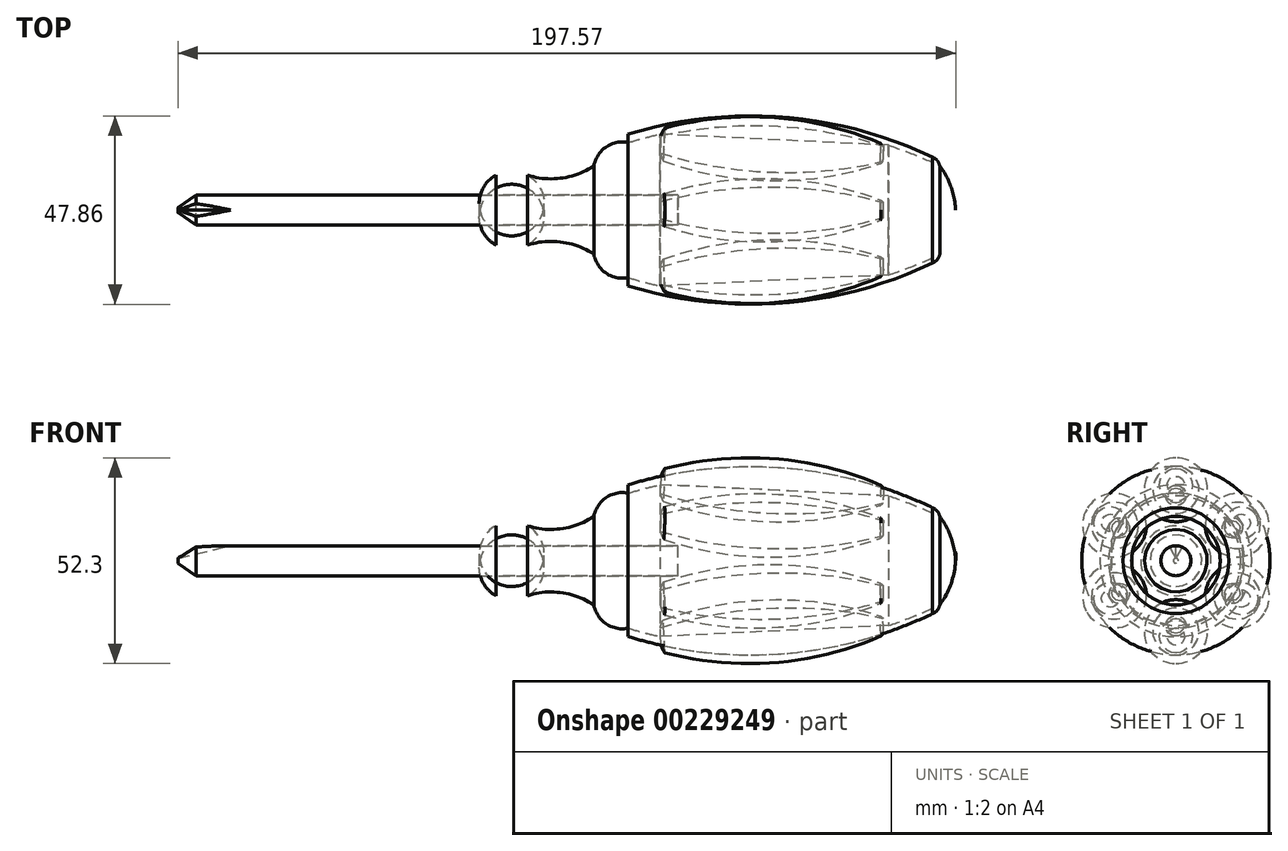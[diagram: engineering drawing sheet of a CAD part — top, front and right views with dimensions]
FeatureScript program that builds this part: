
annotation { "Feature Type Name" : "Feature", "Feature Type Description" : "" }
export const myFeature = defineFeature(function(context is Context, id is Id, definition is map)
    precondition{}
    {
        {
            var Q0;
            Q0=qCreatedBy(makeId("Front.planeOp"),FACE);
            var sketch = newSketch(context, id + "F0", { "sketchPlane" : qUnion([Q0])});
            skLineSegment(sketch, "E0", {"start": v(-80.73, 0) * mm, "end": v(-80.73, 0.63) * mm});
            skLineSegment(sketch, "E1", {"start": v(-80.73, 0.63) * mm, "end": v(-76.2, 3.8) * mm});
            skLineSegment(sketch, "E2", {"start": v(-76.2, 3.8) * mm, "end": v(46.27, 3.8) * mm});
            skLineSegment(sketch, "E3", {"start": v(46.27, 3.8) * mm, "end": v(46.27, 0) * mm});
            skLineSegment(sketch, "E4", {"start": v(46.27, 0) * mm, "end": v(-80.73, 0) * mm});
            skLineSegment(sketch, "E5", {"start": v(0, 3.8) * mm, "end": v(0, 8.89) * mm});
            skArc(sketch, "E6", {"start": v(8.04, 8.89) * mm, "mid": v(4.02, 9.93) * mm, "end": v(0, 8.89) * mm});
            skArc(sketch, "E7", {"start": v(8.04, 8.89) * mm, "mid": v(16.73, 8.13) * mm, "end": v(24.89, 11.25) * mm});
            skArc(sketch, "E8", {"start": v(33.62, 17.15) * mm, "mid": v(28, 16.04) * mm, "end": v(24.89, 11.25) * mm});
            skArc(sketch, "E9", {"start": v(112.77, 11.25) * mm, "mid": v(73.75, 21.64) * mm, "end": v(33.62, 17.15) * mm});
            skArc(sketch, "E10", {"start": v(116.81, 0) * mm, "mid": v(115.61, 5.92) * mm, "end": v(112.77, 11.25) * mm});
            skLineSegment(sketch, "E11", {"start": v(33.62, 17.15) * mm, "end": v(33.62, 19.29) * mm});
            skArc(sketch, "E12", {"start": v(110.93, 13.46) * mm, "mid": v(72.82, 23.62) * mm, "end": v(33.62, 19.29) * mm});
            skArc(sketch, "E13", {"start": v(42.94, 23.4) * mm, "mid": v(41.95, 21.46) * mm, "end": v(41.69, 19.29) * mm});
            skArc(sketch, "E14", {"start": v(97.82, 19.15) * mm, "mid": v(70.74, 25.9) * mm, "end": v(42.94, 23.4) * mm});
            skArc(sketch, "E15", {"start": v(99.75, 16.47) * mm, "mid": v(98.95, 17.93) * mm, "end": v(97.82, 19.15) * mm});
            skLineSegment(sketch, "E16", {"start": v(41.69, 19.29) * mm, "end": v(99.75, 16.47) * mm});
            skLineSegment(sketch, "E17", {"start": v(46.27, 0) * mm, "end": v(116.81, 0) * mm});
            skLineSegment(sketch, "E18", {"start": v(8.04, 8.89) * mm, "end": v(8.04, 3.8) * mm, "construction": true});
            skLineSegment(sketch, "E19", {"start": v(24.89, 11.25) * mm, "end": v(24.89, 3.8) * mm, "construction": true});
            skLineSegment(sketch, "E20", {"start": v(33.62, 17.15) * mm, "end": v(33.62, 3.8) * mm, "construction": true});
            skArc(sketch, "E21", {"start": v(112.77, 11.25) * mm, "mid": v(112.13, 12.59) * mm, "end": v(110.93, 13.46) * mm});
            skLineSegment(sketch, "E22", {"start": v(112.77, 11.25) * mm, "end": v(112.77, 0) * mm, "construction": true});
            skLineSegment(sketch, "E23", {"start": v(48.03, 19.6) * mm, "end": v(48.03, 0) * mm, "construction": true});
            skLineSegment(sketch, "E24", {"start": v(42.94, 23.4) * mm, "end": v(42.94, 0) * mm, "construction": true});
            skLineSegment(sketch, "E25", {"start": v(97.82, 19.15) * mm, "end": v(97.82, 0) * mm, "construction": true});
            skLineSegment(sketch, "E26", {"start": v(110.93, 13.46) * mm, "end": v(110.93, 0) * mm, "construction": true});
            skSolve(sketch);
        }
        {
            var Q0;
            {var subQ5=sQuery(id+"F0.wireOp",EDGE,"E14");Q0=makeQuery(id+"F0.imprint","IMPRINT",FACE,{"disambiguationData":[TD([[makeQuery(id+"F0.imprint","IMPRINT",EDGE,{"derivedFrom":subQ5}),1.0]])]});}
            var Q1;
            Q1=sQuery(id+"F0.wireOp",EDGE,"E16");
            revolve(context, id + "F1", {"entities" : qUnion([Q0]), "axis" : qUnion([Q1]), "revolveType" : RevolveType.FULL});
        }
        {
            var Q0;
            Q0=makeQuery(id+"F0.imprint","IMPRINT",FACE,{"disambiguationData":[TD([[makeQuery(id+"F0.imprint","IMPRINT",EDGE,{"derivedFrom":sQuery(id+"F0.wireOp",EDGE,"E0")}),-1.0]])]});
            var Q1;
            Q1=sQuery(id+"F0.wireOp",EDGE,"E4");
            revolve(context, id + "F2", {"entities" : qUnion([Q0]), "axis" : qUnion([Q1]), "revolveType" : RevolveType.FULL});
        }
        {
            var Q0;
            {var subQ3=sQuery(id+"F0.wireOp",EDGE,"E3");Q0=makeQuery(id+"F0.imprint","IMPRINT",FACE,{"disambiguationData":[TD([[makeQuery(id+"F0.imprint","IMPRINT",EDGE,{"derivedFrom":subQ3}),1.0]])]});}
            var Q1;
            Q1=sQuery(id+"F0.wireOp",EDGE,"E17");
            revolve(context, id + "F3", {"entities" : qUnion([Q0]), "axis" : qUnion([Q1]), "revolveType" : RevolveType.FULL});
        }
        {
            var Q0;
            {var subQ0=sQuery(id+"F0.wireOp",EDGE,"E11");Q0=makeQuery(id+"F0.imprint","IMPRINT",FACE,{"disambiguationData":[TD([[makeQuery(id+"F0.imprint","IMPRINT",EDGE,{"derivedFrom":subQ0}),-1.0]])]});}
            var Q1;
            {var subQ0=sQuery(id+"F0.wireOp",EDGE,"E16");Q1=makeQuery(id+"F0.imprint","IMPRINT",FACE,{"disambiguationData":[TD([[makeQuery(id+"F0.imprint","IMPRINT",EDGE,{"derivedFrom":subQ0}),1.0]])]});}
            var Q2;
            {var subQ4=sQuery(id+"F0.wireOp",EDGE,"E15");var subQ6=sQuery(id+"F0.wireOp",EDGE,"E12");var subQ7=makeQuery(id+"F0.imprint","INTERSECT",VERTEX,{"derivedFrom":[subQ6,subQ4]});Q2=makeQuery(id+"F0.imprint","IMPRINT",FACE,{"disambiguationData":[TD([[makeQuery(id+"F0.imprint","IMPRINT",EDGE,{"disambiguationData":[TD([[subQ7,-1.0]])],"derivedFrom":subQ6}),1.0]])]});}
            var Q3;
            {var subQ0=sQuery(id+"F0.wireOp",EDGE,"E21");Q3=makeQuery(id+"F0.imprint","IMPRINT",FACE,{"disambiguationData":[TD([[makeQuery(id+"F0.imprint","IMPRINT",EDGE,{"derivedFrom":subQ0}),1.0]])]});}
            var Q4;
            Q4=sQuery(id+"F0.wireOp",EDGE,"E17");
            revolve(context, id + "F4", {"entities" : qUnion([Q0, Q1, Q2, Q3]), "axis" : qUnion([Q4]), "revolveType" : RevolveType.FULL});
        }
        {
            var Q0;
            Q0=makeQuery(id+"F1.opRevolve","SWEPT_BODY",BODY,{"disambiguationData":[OSD([sQuery(id+"F0.wireOp",EDGE,"E12"),sQuery(id+"F0.wireOp",EDGE,"E13"),sQuery(id+"F0.wireOp",EDGE,"E14"),sQuery(id+"F0.wireOp",EDGE,"E15")])]});
            var Q1;
            Q1=sQuery(id+"F0.wireOp",EDGE,"E17");
            circularPattern(context, id + "F5", {"entities" : qUnion([Q0]), "axis" : qUnion([Q1]), "angle" : 360 * degree, "instanceCount" : 6, "equalSpace" : true});
        }
        {
            var Q0;
            Q0=qCreatedBy(makeId("Front.planeOp"),FACE);
            var sketch = newSketch(context, id + "F6", { "sketchPlane" : qUnion([Q0])});
            skLineSegment(sketch, "E27.0", {"start": v(-76.2, 3.8) * mm, "end": v(-76.2, -3.8) * mm});
            skPoint(sketch, "E28.0", {"position": v(-80.73, 0) * mm});
            skPoint(sketch, "E29.0", {"position": v(-80.73, 0.63) * mm});
            skLineSegment(sketch, "E30", {"start": v(-80.73, 0.63) * mm, "end": v(-76.2, 3.8) * mm});
            skLineSegment(sketch, "E31", {"start": v(-76.2, -3.8) * mm, "end": v(-80.73, -0.63) * mm});
            skLineSegment(sketch, "E32.0", {"start": v(-76.2, 3.8) * mm, "end": v(-67.42, 3.8) * mm, "construction": true});
            skLineSegment(sketch, "E33", {"start": v(-80.73, 0.63) * mm, "end": v(-67.42, 3.8) * mm});
            skPoint(sketch, "E34.orphan", {"position": v(46.27, 3.8) * mm});
            skPoint(sketch, "E35.orphan", {"position": v(-80.73, -0.63) * mm});
            skLineSegment(sketch, "E36", {"start": v(-80.73, 0.63) * mm, "end": v(-83.47, 6.76) * mm, "construction": true});
            skSolve(sketch);
        }
        {
            var Q0;
            Q0=qCreatedBy(makeId("Top.planeOp"),FACE);
            var Q1;
            Q1=sQuery(id+"F6.wireOp",EDGE,"E36");
            cPlane(context, id + "F7", {"entities" : qUnion([Q0, Q1]), "cplaneType" : CPlaneType.LINE_ANGLE, "offset" : 25.4 * mm, "angle" : 0 * degree, "width" : 152.4 * mm, "height" : 152.4 * mm});
        }
        {
            var Q0;
            Q0=qCreatedBy(id+"F7.planeOp",FACE);
            var sketch = newSketch(context, id + "F8", { "sketchPlane" : qUnion([Q0])});
            skLineSegment(sketch, "E37", {"start": v(0, 33.49) * mm, "end": v(7.4, 41.46) * mm});
            skLineSegment(sketch, "E38", {"start": v(7.4, 41.46) * mm, "end": v(-7.84, 41.46) * mm});
            skLineSegment(sketch, "E39", {"start": v(0, 33.49) * mm, "end": v(-7.84, 41.46) * mm});
            skEllipse(sketch, "E40.0", {"center": v(0, 32.9) * mm, "majorRadius": 0.63 * mm, "minorRadius": 0.58 * mm, "majorAxis": v(-1, 0)});
            skPoint(sketch, "E41.0", {"position": v(0, 33.49) * mm});
            skSolve(sketch);
        }
        {
            var Q0;
            Q0=makeQuery(id+"F8.imprint","IMPRINT",FACE,{"disambiguationData":[TD([[makeQuery(id+"F8.imprint","IMPRINT",EDGE,{"derivedFrom":sQuery(id+"F8.wireOp",EDGE,"E37")}),1.0]])]});
            var Q1;
            Q1=sQuery(id+"F6.wireOp",EDGE,"E33");
            sweep(context, id + "F9", {"operationType" : NewBodyOperationType.REMOVE, "profiles" : qUnion([Q0]), "path" : qUnion([Q1])});
        }
    });
